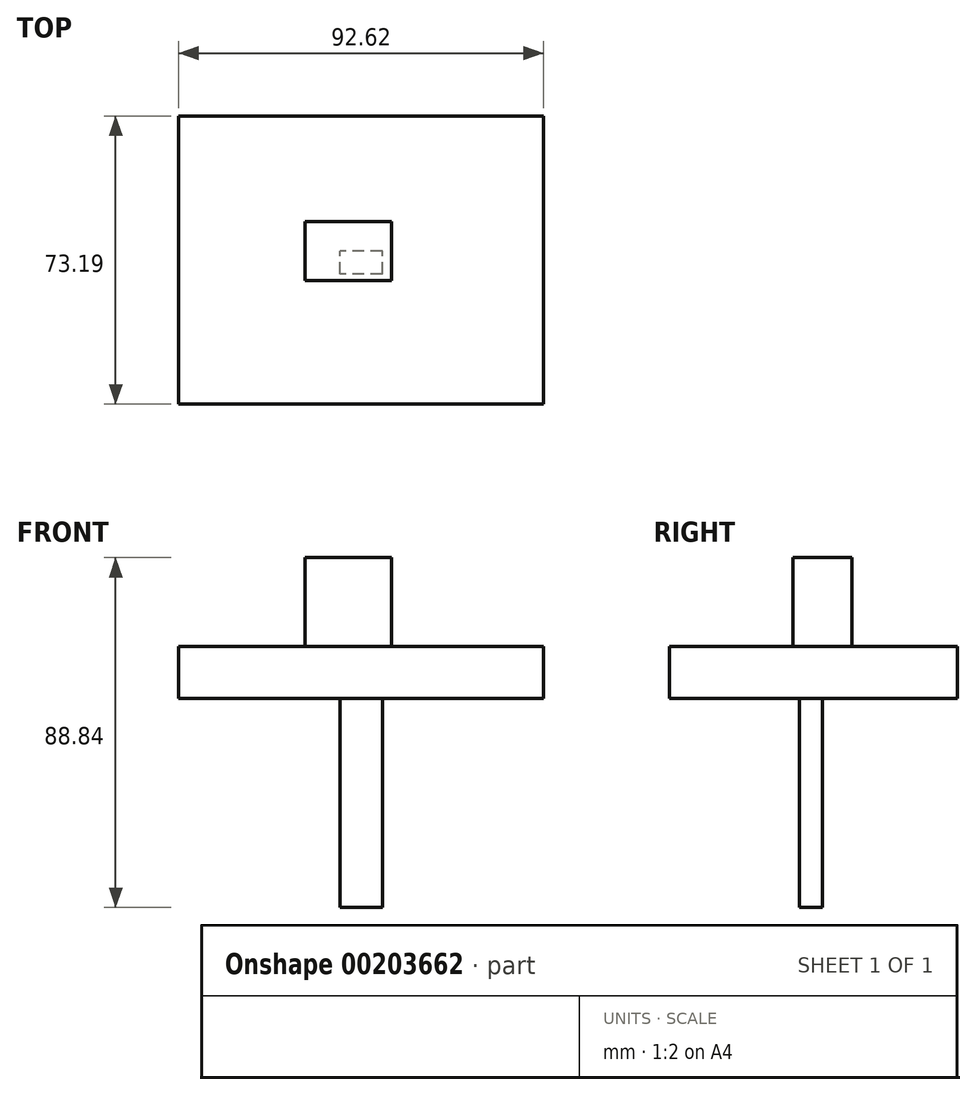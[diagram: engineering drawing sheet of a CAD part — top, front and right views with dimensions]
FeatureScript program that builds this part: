
annotation { "Feature Type Name" : "Feature", "Feature Type Description" : "" }
export const myFeature = defineFeature(function(context is Context, id is Id, definition is map)
    precondition{}
    {
        {
            var Q0;
            Q0=qCreatedBy(makeId("Front.planeOp"),FACE);
            var sketch = newSketch(context, id + "F0", { "sketchPlane" : qUnion([Q0])});
            skLineSegment(sketch, "E0.bottom", {"start": v(5.4, 33.17) * mm, "end": v(-5.4, 33.17) * mm});
            skLineSegment(sketch, "E0.top", {"start": v(5.4, -33.17) * mm, "end": v(-5.4, -33.17) * mm});
            skLineSegment(sketch, "E0.left", {"start": v(5.4, 33.17) * mm, "end": v(5.4, -33.17) * mm});
            skLineSegment(sketch, "E0.right", {"start": v(-5.4, 33.17) * mm, "end": v(-5.4, -33.17) * mm});
            skPoint(sketch, "E0.middle", {"position": v(0, 0) * mm});
            skSolve(sketch);
        }
        {
            var Q0;
            Q0=makeQuery(id+"F0.imprint","IMPRINT",FACE,{"disambiguationData":[TD([[makeQuery(id+"F0.imprint","IMPRINT",EDGE,{"derivedFrom":sQuery(id+"F0.wireOp",EDGE,"E0.bottom")}),1.0]])]});
            extrude(context, id + "F1", {"entities" : qUnion([Q0]), "depth" : 5.8 * mm});
        }
        {
            var Q0;
            Q0=makeQuery(id+"F1.opExtrude","SWEPT_FACE",FACE,{"disambiguationData":[OSD([sQuery(id+"F0.wireOp",EDGE,"E0.bottom")])]});
            var sketch = newSketch(context, id + "F2", { "sketchPlane" : qUnion([Q0])});
            skLineSegment(sketch, "E1.bottom", {"start": v(46.31, 34.3) * mm, "end": v(-46.31, 34.3) * mm});
            skLineSegment(sketch, "E1.top", {"start": v(46.31, -38.9) * mm, "end": v(-46.31, -38.9) * mm});
            skLineSegment(sketch, "E1.left", {"start": v(46.31, 34.3) * mm, "end": v(46.31, -38.9) * mm});
            skLineSegment(sketch, "E1.right", {"start": v(-46.31, 34.3) * mm, "end": v(-46.31, -38.9) * mm});
            skPoint(sketch, "E1.middle", {"position": v(0, -2.3) * mm});
            skPoint(sketch, "E1.middle.positionSnap0", {"position": v(0, -5.8) * mm});
            skPoint(sketch, "E1.centerSnap0", {"position": v(0, -5.8) * mm});
            skSolve(sketch);
        }
        {
            var Q0;
            Q0=makeQuery(id+"F2.imprint","IMPRINT",FACE,{"disambiguationData":[TD([[makeQuery(id+"F2.imprint","IMPRINT",EDGE,{"derivedFrom":sQuery(id+"F2.wireOp",EDGE,"E1.bottom")}),1.0]])]});
            extrude(context, id + "F3", {"entities" : qUnion([Q0]), "operationType" : NewBodyOperationType.ADD, "oppositeDirection" : true, "depth" : 13.2 * mm});
        }
        {
            var Q0;
            {var subQ0=sQuery(id+"F0.wireOp",EDGE,"E0.bottom");Q0=makeQuery(id+"F3.boolean.opBoolean","MERGE",FACE,{"derivedFrom":[makeQuery(id+"F1.opExtrude","SWEPT_FACE",FACE,{"disambiguationData":[OSD([subQ0])]}),makeQuery(id+"F3.opExtrude","CAP_FACE",FACE,{"disambiguationData":[OSD([subQ0,sQuery(id+"F0.wireOp",EDGE,"E0.left"),sQuery(id+"F0.wireOp",EDGE,"E0.right"),sQuery(id+"F2.wireOp",EDGE,"E1.bottom"),sQuery(id+"F2.wireOp",EDGE,"E1.top"),sQuery(id+"F2.wireOp",EDGE,"E1.left"),sQuery(id+"F2.wireOp",EDGE,"E1.right")])],"isStart":true})]});}
            var sketch = newSketch(context, id + "F4", { "sketchPlane" : qUnion([Q0])});
            skLineSegment(sketch, "E2.bottom", {"start": v(-14.25, 7.5) * mm, "end": v(7.75, 7.5) * mm});
            skLineSegment(sketch, "E2.top", {"start": v(-14.25, -7.5) * mm, "end": v(7.75, -7.5) * mm});
            skLineSegment(sketch, "E2.left", {"start": v(-14.25, 7.5) * mm, "end": v(-14.25, -7.5) * mm});
            skLineSegment(sketch, "E2.right", {"start": v(7.75, 7.5) * mm, "end": v(7.75, -7.5) * mm});
            skPoint(sketch, "E2.middle", {"position": v(-3.25, 0) * mm});
            skSolve(sketch);
        }
        {
            var Q0;
            Q0 = qSketchRegion(id + "F4", true);
            extrude(context, id + "F5", {"entities" : qUnion([Q0]), "operationType" : NewBodyOperationType.ADD, "depth" : 22.5 * mm});
        }
    });
